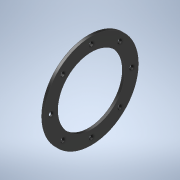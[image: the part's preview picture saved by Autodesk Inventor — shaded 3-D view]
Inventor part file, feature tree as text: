
AUTODESK INVENTOR PART (.ipt)
format: ipt  version: 2020 (Build 240168000, 168)  size: 159,744 bytes
history: native  units: mm
features: sketch x4, extrude x3, hole x1, pattern_circular x1
ambient origin geometry x8: Origin, YZ Plane, XZ Plane, XY Plane, X Axis, Y Axis, Z Axis, Center Point
bodies: Solid1 (feature_tree)
feature tree (9):
  extrude  "Extrusion1"  Depth=175.0mm
  extrude  "Extrusion2"  Depth=10.0mm TaperAngle=0.0deg
  hole  "Hole1"  [1 undecoded]
  pattern_circular  "Circular Pattern1"  Count=15  [1 undecoded]
  extrude  "Extrusion3"  Depth=8.5mm TaperAngle=360.0deg
  sketch  "Sketch1"  dims[d0=175.0mm d1=175.0mm]
  sketch  "Sketch2"  dims[d2=350.0mm d3=10.0mm d4=0.0mm]
  sketch  "Sketch3"  dims[d5=250.0mm d6=0.0mm d7=0.0mm d8=150.0mm]
  sketch  "Sketch5"  dims[d9=0.0mm d10=17.0mm d11=16.0mm d12=4.0mm d13=2.0mm d14=90.0deg d15=8.0mm d16=20.594885mm d17=80.0mm d18=360.0deg d30=3.490659mm d31=150.0mm d32=8.5mm d33=8.5mm d34=8.5mm d35=8.5mm d36=5.0mm d37=0.0mm d38=3.490659mm d39=150.0mm d40=8.5mm d41=8.5mm d42=8.5mm d43=8.5mm]
note: 2 required parameter values undecoded (feature->parameter linkage not recoverable at this tier; creation-order binding heuristic only, values carry confidence <= 0.55)
